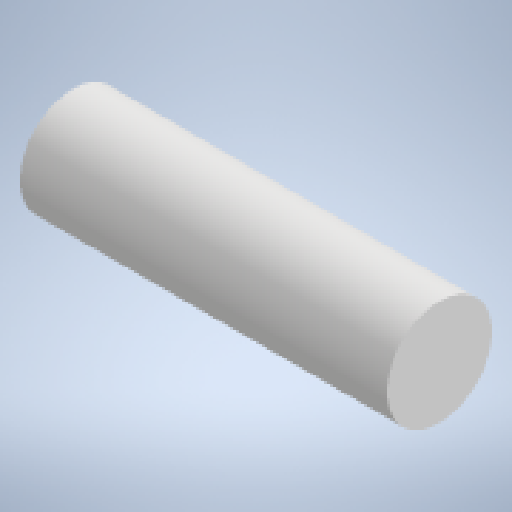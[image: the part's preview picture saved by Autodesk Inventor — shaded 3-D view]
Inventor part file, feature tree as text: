
AUTODESK INVENTOR PART (.ipt)
format: ipt  version: 2025 (Build 290162010, 162A)  size: 129,024 bytes
history: native  units: mm
features: extrude x1, sketch x1
ambient origin geometry x8: Origin, YZ Plane, XZ Plane, XY Plane, X Axis, Y Axis, Z Axis, Center Point
bodies: Volumenkörper1 (feature_tree)
feature tree (2):
  extrude  "Extrusion1"  Depth=50.5mm TaperAngle=0.0deg
  sketch  "Skizze1"  dims[d0=14.5mm d1=50.5mm d2=0.0mm]
